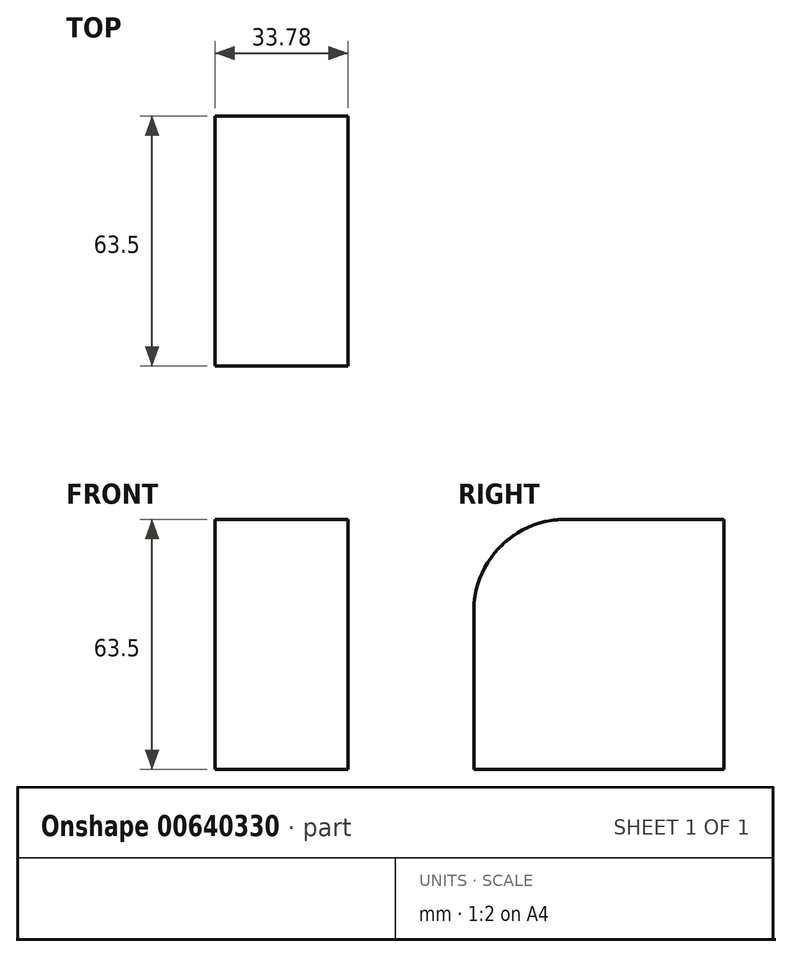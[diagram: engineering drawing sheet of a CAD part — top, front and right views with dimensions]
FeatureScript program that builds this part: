
annotation { "Feature Type Name" : "Feature", "Feature Type Description" : "" }
export const myFeature = defineFeature(function(context is Context, id is Id, definition is map)
    precondition{}
    {
        {
            var Q0;
            Q0=qCreatedBy(makeId("Top.planeOp"),FACE);
            var sketch = newSketch(context, id + "F0", { "sketchPlane" : qUnion([Q0])});
            skLineSegment(sketch, "E0.bottom", {"start": v(-27, 37.78) * mm, "end": v(6.78, 37.78) * mm});
            skLineSegment(sketch, "E0.top", {"start": v(-27, -25.72) * mm, "end": v(6.78, -25.72) * mm});
            skLineSegment(sketch, "E0.left", {"start": v(-27, 37.78) * mm, "end": v(-27, -25.72) * mm});
            skLineSegment(sketch, "E0.right", {"start": v(6.78, 37.78) * mm, "end": v(6.78, -25.72) * mm});
            skSolve(sketch);
        }
        {
            var Q0;
            Q0=makeQuery(id+"F0.imprint","IMPRINT",FACE,{"disambiguationData":[TD([[makeQuery(id+"F0.imprint","IMPRINT",EDGE,{"derivedFrom":sQuery(id+"F0.wireOp",EDGE,"E0.bottom")}),-1.0]])]});
            extrude(context, id + "F1", {"entities" : qUnion([Q0]), "depth" : 63.5 * mm, "offsetDistance" : 25.4 * mm});
        }
        {
            var Q0;
            Q0=makeQuery(id+"F1.opExtrude","CAP_EDGE",EDGE,{"disambiguationData":[OSD([sQuery(id+"F0.wireOp",EDGE,"E0.top")])],"isStart":false});
            fillet(context, id + "F2", {"entities" : qUnion([Q0]), "radius" : 22.7 * mm, "tangentPropagation" : true, "rho" : 0.4, "crossSection" : FilletCrossSection.CONIC, "allowEdgeOverflow" : false});
        }
    });
